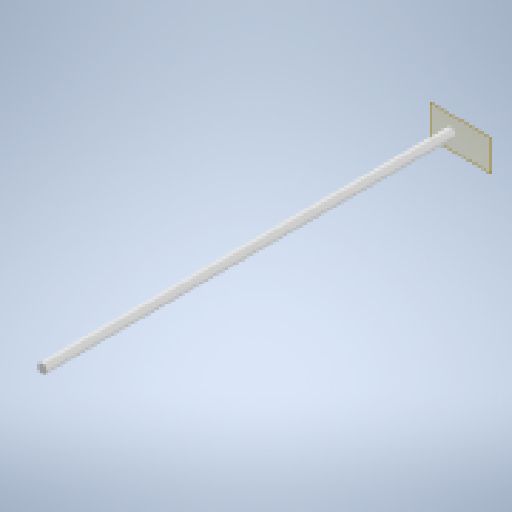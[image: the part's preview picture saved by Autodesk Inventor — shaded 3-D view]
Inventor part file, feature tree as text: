
AUTODESK INVENTOR PART (.ipt)
format: ipt  version: 2025 (Build 290162000, 162)  size: 141,824 bytes
history: native  units: in
note: dims shown in document units (in); Inventor stores cm internally (conversion verified against a paired STEP export)
features: other x2, plane x1, extrude x1, sketch x1, reference x1
ambient origin geometry x8: Origin, YZ Plane, XZ Plane, XY Plane, X Axis, Y Axis, Z Axis, Center Point
bodies: Solid1 (feature_tree)
feature tree (6):
  plane  "Work Plane1"
  extrude  "Extrusion1"  Depth=0.5in
  sketch  "Sketch1"  dims[d0=1.0in d1=9.0in d2=44.0in d3=0.0in d4=1.3in d5=0.0344in d6=0.5in d7=0.0344in]
  reference  "Reference1"
  other  "UAV_Assembly_1.0.iam"
  other  "WingBox:1"
